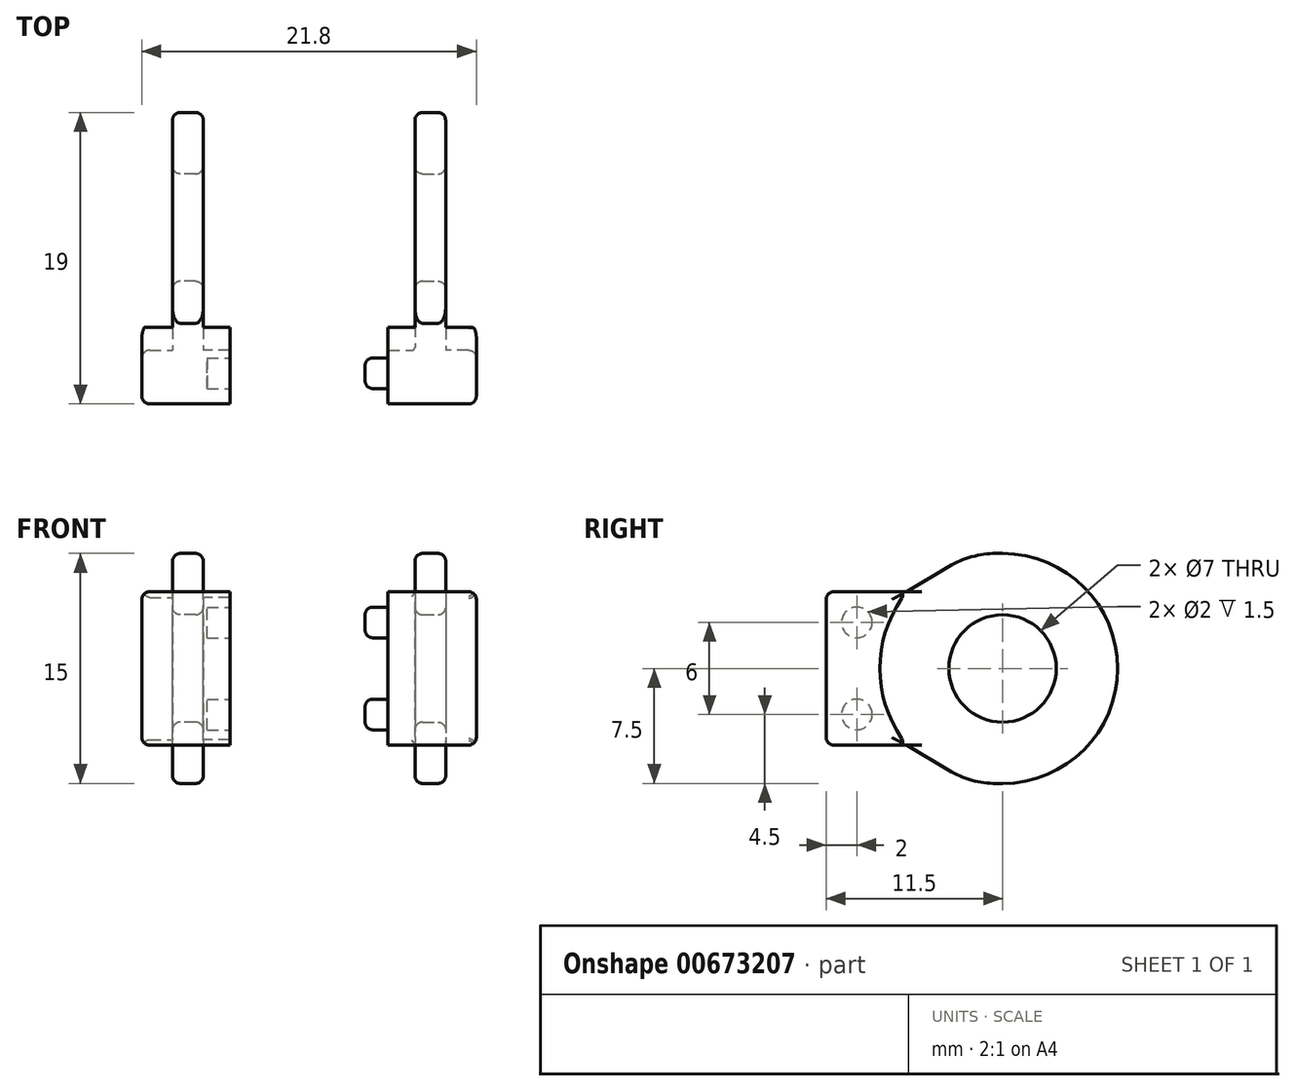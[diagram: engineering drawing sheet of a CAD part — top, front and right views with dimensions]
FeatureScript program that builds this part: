
annotation { "Feature Type Name" : "Feature", "Feature Type Description" : "" }
export const myFeature = defineFeature(function(context is Context, id is Id, definition is map)
    precondition{}
    {
        {
            var Q0;
            Q0=qCreatedBy(makeId("Right.planeOp"),FACE);
            var sketch = newSketch(context, id + "F0", { "sketchPlane" : qUnion([Q0])});
            skArc(sketch, "E0", {"start": v(0, -7.5) * mm, "mid": v(7.5, 0) * mm, "end": v(0, 7.5) * mm});
            skLineSegment(sketch, "E1", {"start": v(0, -7.5) * mm, "end": v(-0.42, -7.5) * mm});
            skLineSegment(sketch, "E2", {"start": v(-10, -5) * mm, "end": v(-10, 5) * mm});
            skLineSegment(sketch, "E3", {"start": v(-0.42, 7.5) * mm, "end": v(0, 7.5) * mm});
            skCircle(sketch, "E4", {"center": v(0, 0) * mm, "radius": 3.5 * mm});
            skCircle(sketch, "E5", {"center": v(0, 0) * mm, "radius": 7.5 * mm, "construction": true});
            skArc(sketch, "E6", {"start": v(-6.52, 4.63) * mm, "mid": v(-8, 0) * mm, "end": v(-6.52, -4.63) * mm});
            skLineSegment(sketch, "E7", {"start": v(-10, 0) * mm, "end": v(-10, 5) * mm, "construction": true});
            skLineSegment(sketch, "E8", {"start": v(-10, 5) * mm, "end": v(-6.24, 5) * mm});
            skLineSegment(sketch, "E9", {"start": v(-6.24, 5) * mm, "end": v(-3.5, 6.65) * mm});
            skLineSegment(sketch, "E10", {"start": v(-10, 0) * mm, "end": v(-13.42, 0) * mm, "construction": true});
            skLineSegment(sketch, "E11.MirrorCS", {"start": v(-10, -5) * mm, "end": v(-6.24, -5) * mm});
            skLineSegment(sketch, "E12.MirrorCS", {"start": v(-6.24, -5) * mm, "end": v(-3.5, -6.65) * mm});
            skPoint(sketch, "E13.start.orphan", {"position": v(-5, -7.5) * mm});
            skPoint(sketch, "E14.orphan", {"position": v(-10, -7.5) * mm});
            skPoint(sketch, "E15.orphan", {"position": v(-10, 7.5) * mm});
            skPoint(sketch, "E16.orphan", {"position": v(-5, 7.5) * mm});
            skPoint(sketch, "E17.visualSharp", {"position": v(-2.08, 7.5) * mm});
            skArc(sketch, "E17.filletArc", {"start": v(-0.42, 7.5) * mm, "mid": v(-2.02, 7.28) * mm, "end": v(-3.5, 6.65) * mm});
            skPoint(sketch, "E18.visualSharp", {"position": v(-2.08, -7.5) * mm});
            skArc(sketch, "E18.filletArc", {"start": v(-3.5, -6.65) * mm, "mid": v(-2.02, -7.28) * mm, "end": v(-0.42, -7.5) * mm});
            skLineSegment(sketch, "E19", {"start": v(-6.52, 5) * mm, "end": v(-6.52, 4.63) * mm});
            skLineSegment(sketch, "E20.MirrorCS", {"start": v(-3.04, 0) * mm, "end": v(0.38, 0) * mm, "construction": true});
            skLineSegment(sketch, "E21.MirrorCS", {"start": v(-6.52, -5) * mm, "end": v(-6.52, -4.63) * mm});
            skSolve(sketch);
        }
        {
            var Q0;
            Q0=makeQuery(id+"F0.imprint","IMPRINT",FACE,{"disambiguationData":[TD([[makeQuery(id+"F0.imprint","IMPRINT",EDGE,{"derivedFrom":sQuery(id+"F0.wireOp",EDGE,"E0")}),1.0]])]});
            var Q1;
            {var subQ1=sQuery(id+"F0.wireOp",EDGE,"E2");Q1=makeQuery(id+"F0.imprint","IMPRINT",FACE,{"disambiguationData":[TD([[makeQuery(id+"F0.imprint","IMPRINT",EDGE,{"derivedFrom":subQ1}),-1.0]])]});}
            extrude(context, id + "F1", {"entities" : qUnion([Q0, Q1]), "depth" : 1 * mm});
        }
        {
            var Q0;
            {var subQ1=sQuery(id+"F0.wireOp",EDGE,"E2");Q0=makeQuery(id+"F0.imprint","IMPRINT",FACE,{"disambiguationData":[TD([[makeQuery(id+"F0.imprint","IMPRINT",EDGE,{"derivedFrom":subQ1}),-1.0]])]});}
            extrude(context, id + "F2", {"entities" : qUnion([Q0]), "operationType" : NewBodyOperationType.ADD, "depth" : 2.75 * mm});
        }
        {
            var Q0;
            {var subQ1=sQuery(id+"F0.wireOp",EDGE,"E2");Q0=makeQuery(id+"F0.imprint","IMPRINT",FACE,{"disambiguationData":[TD([[makeQuery(id+"F0.imprint","IMPRINT",EDGE,{"derivedFrom":subQ1}),-1.0]])]});}
            extrude(context, id + "F3", {"entities" : qUnion([Q0]), "operationType" : NewBodyOperationType.ADD, "oppositeDirection" : true, "depth" : 3 * mm});
        }
        {
            var Q0;
            {var subQ0=sQuery(id+"F0.wireOp",EDGE,"E2");Q0=makeQuery(id+"F3.boolean.opBoolean","MERGE",FACE,{"derivedFrom":[makeQuery(id+"F2.boolean.opBoolean","MERGE",FACE,{"derivedFrom":[makeQuery(id+"F1.opExtrude","SWEPT_FACE",FACE,{"disambiguationData":[OSD([subQ0])]}),makeQuery(id+"F2.opExtrude","SWEPT_FACE",FACE,{"disambiguationData":[OSD([subQ0])]})]}),makeQuery(id+"F3.opExtrude","SWEPT_FACE",FACE,{"disambiguationData":[OSD([subQ0])]})]});}
            extrude(context, id + "F4", {"entities" : qUnion([Q0]), "operationType" : NewBodyOperationType.ADD, "depth" : 1.5 * mm});
        }
        {
            var Q0;
            {var subQ0=sQuery(id+"F0.wireOp",EDGE,"E2");Q0=makeQuery(id+"F4.boolean.opBoolean","MERGE",FACE,{"derivedFrom":[makeQuery(id+"F2.opExtrude","CAP_FACE",FACE,{"disambiguationData":[OSD([sQuery(id+"F0.wireOp",EDGE,"E1"),subQ0,sQuery(id+"F0.wireOp",EDGE,"E3"),sQuery(id+"F0.wireOp",EDGE,"E6"),sQuery(id+"F0.wireOp",EDGE,"eQNor3UN-66I8-VjKn-XfJS-KKaY8PZ4G21v"),sQuery(id+"F0.wireOp",EDGE,"E13")])],"isStart":false}),makeQuery(id+"F4.opExtrude","SWEPT_FACE",FACE,{"disambiguationData":[OSD([subQ0]),TDD([makeQuery(id+"F2.opExtrude","CAP_EDGE",EDGE,{"disambiguationData":[OSD([subQ0])],"isStart":false})])]})]});}
            var sketch = newSketch(context, id + "F5", { "sketchPlane" : qUnion([Q0])});
            skCircle(sketch, "E22", {"center": v(-9.5, 3) * mm, "radius": 1 * mm});
            skLineSegment(sketch, "E23", {"start": v(-8, 0) * mm, "end": v(-11.5, 0) * mm, "construction": true});
            skCircle(sketch, "E24.MirrorC", {"center": v(-9.5, -3) * mm, "radius": 1 * mm});
            skSolve(sketch);
        }
        {
            var Q0;
            Q0=qSketchRegion(id+"F5",true);
            extrude(context, id + "F6", {"entities" : qUnion([Q0]), "operationType" : NewBodyOperationType.REMOVE, "oppositeDirection" : true, "depth" : 1.5 * mm});
        }
        {
            var Q0;
            Q0=qCreatedBy(makeId("Right.planeOp"),FACE);
            cPlane(context, id + "F7", {"entities" : qUnion([Q0]), "cplaneType" : CPlaneType.OFFSET, "offset" : 7.9 * mm, "width" : 150 * mm, "height" : 150 * mm});
        }
        {
            var Q0;
            Q0=makeQuery(id+"F1.opExtrude","SWEPT_BODY",BODY,{"disambiguationData":[OSD([sQuery(id+"F0.wireOp",EDGE,"E0"),sQuery(id+"F0.wireOp",EDGE,"E1"),sQuery(id+"F0.wireOp",EDGE,"E2"),sQuery(id+"F0.wireOp",EDGE,"E3"),sQuery(id+"F0.wireOp",EDGE,"E4")])]});
            var Q1;
            Q1=qCreatedBy(id+"F7.planeOp",FACE);
            mirror(context, id + "F8", {"entities" : qUnion([Q0]), "mirrorPlane" : qUnion([Q1])});
        }
        {
            var Q0;
            Q0=makeQuery(id+"F8.opPattern","COPY",FACE,{"derivedFrom":makeQuery(id+"F6.boolean.opBoolean","COPY",FACE,{"derivedFrom":makeQuery(id+"F6.opExtrude","CAP_FACE",FACE,{"disambiguationData":[OSD([sQuery(id+"F5.wireOp",EDGE,"E22")])],"isStart":false})}),"instanceName":"1"});
            var Q1;
            Q1=makeQuery(id+"F8.opPattern","COPY",FACE,{"derivedFrom":makeQuery(id+"F6.boolean.opBoolean","COPY",FACE,{"derivedFrom":makeQuery(id+"F6.opExtrude","CAP_FACE",FACE,{"disambiguationData":[OSD([sQuery(id+"F5.wireOp",EDGE,"E24.MirrorC")])],"isStart":false})}),"instanceName":"1"});
            extrude(context, id + "F9", {"entities" : qUnion([Q0, Q1]), "operationType" : NewBodyOperationType.ADD, "depth" : 3 * mm});
        }
        {
            var Q0;
            Q0=makeQuery(id+"F1.opExtrude","CAP_FACE",FACE,{"disambiguationData":[OSD([sQuery(id+"F0.wireOp",EDGE,"E0"),sQuery(id+"F0.wireOp",EDGE,"E1"),sQuery(id+"F0.wireOp",EDGE,"E2"),sQuery(id+"F0.wireOp",EDGE,"E3"),sQuery(id+"F0.wireOp",EDGE,"E4")])],"isStart":true});
            extrude(context, id + "F10", {"entities" : qUnion([Q0]), "operationType" : NewBodyOperationType.ADD, "depth" : 1 * mm});
        }
        {
            var Q0;
            Q0=makeQuery(id+"F8.opPattern","COPY",FACE,{"derivedFrom":makeQuery(id+"F1.opExtrude","CAP_FACE",FACE,{"disambiguationData":[OSD([sQuery(id+"F0.wireOp",EDGE,"E0"),sQuery(id+"F0.wireOp",EDGE,"E1"),sQuery(id+"F0.wireOp",EDGE,"E2"),sQuery(id+"F0.wireOp",EDGE,"E3"),sQuery(id+"F0.wireOp",EDGE,"E4")])],"isStart":true}),"instanceName":"1"});
            extrude(context, id + "F11", {"entities" : qUnion([Q0]), "operationType" : NewBodyOperationType.ADD, "depth" : 1 * mm});
        }
        {
            var Q0;
            Q0=makeQuery(id+"F10.opExtrude","CAP_EDGE",EDGE,{"disambiguationData":[OSD([sQuery(id+"F0.wireOp",EDGE,"E0")])],"isStart":false});
            var Q1;
            {var subQ0=sQuery(id+"F0.wireOp",EDGE,"E2");Q1=makeQuery(id+"F4.boolean.opBoolean","MERGE",FACE,{"derivedFrom":[makeQuery(id+"F3.opExtrude","CAP_FACE",FACE,{"disambiguationData":[OSD([subQ0,sQuery(id+"F0.wireOp",EDGE,"E6"),sQuery(id+"F0.wireOp",EDGE,"E8"),sQuery(id+"F0.wireOp",EDGE,"E11.MirrorCS")])],"isStart":false}),makeQuery(id+"F4.opExtrude","SWEPT_FACE",FACE,{"disambiguationData":[OSD([subQ0]),TDD([makeQuery(id+"F3.opExtrude","CAP_EDGE",EDGE,{"disambiguationData":[OSD([subQ0])],"isStart":false})])]})]});}
            var Q2;
            {var subQ0=sQuery(id+"F0.wireOp",EDGE,"E2");Q2=makeQuery(id+"F8.opPattern","COPY",FACE,{"derivedFrom":makeQuery(id+"F4.boolean.opBoolean","MERGE",FACE,{"derivedFrom":[makeQuery(id+"F3.opExtrude","CAP_FACE",FACE,{"disambiguationData":[OSD([subQ0,sQuery(id+"F0.wireOp",EDGE,"E6"),sQuery(id+"F0.wireOp",EDGE,"E8"),sQuery(id+"F0.wireOp",EDGE,"E11.MirrorCS")])],"isStart":false}),makeQuery(id+"F4.opExtrude","SWEPT_FACE",FACE,{"disambiguationData":[OSD([subQ0]),TDD([makeQuery(id+"F3.opExtrude","CAP_EDGE",EDGE,{"disambiguationData":[OSD([subQ0])],"isStart":false})])]})]}),"instanceName":"1"});}
            var Q3;
            Q3=makeQuery(id+"F11.opExtrude","CAP_EDGE",EDGE,{"disambiguationData":[OSD([sQuery(id+"F0.wireOp",EDGE,"E0")])],"isStart":false});
            var Q4;
            Q4=makeQuery(id+"F11.opExtrude","CAP_EDGE",EDGE,{"disambiguationData":[OSD([sQuery(id+"F0.wireOp",EDGE,"E4")])],"isStart":false});
            var Q5;
            Q5=makeQuery(id+"F8.opPattern","COPY",EDGE,{"derivedFrom":makeQuery(id+"F1.opExtrude","CAP_EDGE",EDGE,{"disambiguationData":[OSD([sQuery(id+"F0.wireOp",EDGE,"E4")])],"isStart":false}),"instanceName":"1"});
            var Q6;
            {var subQ0=sQuery(id+"F0.wireOp",EDGE,"E0");Q6=makeQuery(id+"F11.boolean.opBoolean","MERGE",FACE,{"derivedFrom":[makeQuery(id+"F8.opPattern","COPY",FACE,{"derivedFrom":makeQuery(id+"F1.opExtrude","SWEPT_FACE",FACE,{"disambiguationData":[OSD([subQ0])]}),"instanceName":"1"}),makeQuery(id+"F11.opExtrude","SWEPT_FACE",FACE,{"disambiguationData":[OSD([subQ0])]})]});}
            var Q7;
            {var subQ0=sQuery(id+"F0.wireOp",EDGE,"E0");Q7=makeQuery(id+"F10.boolean.opBoolean","MERGE",FACE,{"derivedFrom":[makeQuery(id+"F1.opExtrude","SWEPT_FACE",FACE,{"disambiguationData":[OSD([subQ0])]}),makeQuery(id+"F10.opExtrude","SWEPT_FACE",FACE,{"disambiguationData":[OSD([subQ0])]})]});}
            var Q8;
            Q8=makeQuery(id+"F10.opExtrude","CAP_EDGE",EDGE,{"disambiguationData":[OSD([sQuery(id+"F0.wireOp",EDGE,"E4")])],"isStart":false});
            var Q9;
            Q9=makeQuery(id+"F1.opExtrude","CAP_EDGE",EDGE,{"disambiguationData":[OSD([sQuery(id+"F0.wireOp",EDGE,"E4")])],"isStart":false});
            var Q10;
            Q10=makeQuery(id+"F4.opExtrude","CAP_EDGE",EDGE,{"disambiguationData":[OSD([sQuery(id+"F0.wireOp",EDGE,"E2"),sQuery(id+"F0.wireOp",EDGE,"E8")])],"isStart":false});
            var Q11;
            Q11=makeQuery(id+"F4.opExtrude","CAP_EDGE",EDGE,{"disambiguationData":[OSD([sQuery(id+"F0.wireOp",EDGE,"E2"),sQuery(id+"F0.wireOp",EDGE,"E11.MirrorCS")])],"isStart":false});
            var Q12;
            Q12=makeQuery(id+"F8.opPattern","COPY",EDGE,{"derivedFrom":makeQuery(id+"F4.opExtrude","CAP_EDGE",EDGE,{"disambiguationData":[OSD([sQuery(id+"F0.wireOp",EDGE,"E2"),sQuery(id+"F0.wireOp",EDGE,"E8")])],"isStart":false}),"instanceName":"1"});
            var Q13;
            Q13=makeQuery(id+"F8.opPattern","COPY",EDGE,{"derivedFrom":makeQuery(id+"F4.opExtrude","CAP_EDGE",EDGE,{"disambiguationData":[OSD([sQuery(id+"F0.wireOp",EDGE,"E2"),sQuery(id+"F0.wireOp",EDGE,"E11.MirrorCS")])],"isStart":false}),"instanceName":"1"});
            var Q14;
            Q14=makeQuery(id+"F9.opExtrude","CAP_FACE",FACE,{"disambiguationData":[OSD([sQuery(id+"F5.wireOp",EDGE,"E22")])],"isStart":false});
            var Q15;
            Q15=makeQuery(id+"F9.opExtrude","CAP_FACE",FACE,{"disambiguationData":[OSD([sQuery(id+"F5.wireOp",EDGE,"E24.MirrorC")])],"isStart":false});
            var Q16;
            Q16=makeQuery(id+"F6.boolean.opBoolean","COPY",EDGE,{"derivedFrom":makeQuery(id+"F6.opExtrude","CAP_EDGE",EDGE,{"disambiguationData":[OSD([sQuery(id+"F5.wireOp",EDGE,"E22")])],"isStart":true})});
            var Q17;
            Q17=makeQuery(id+"F6.boolean.opBoolean","COPY",EDGE,{"derivedFrom":makeQuery(id+"F6.opExtrude","CAP_EDGE",EDGE,{"disambiguationData":[OSD([sQuery(id+"F5.wireOp",EDGE,"E24.MirrorC")])],"isStart":true})});
            fillet(context, id + "F12", {"entities" : qUnion([Q0, Q1, Q2, Q3, Q4, Q5, Q6, Q7, Q8, Q9, Q10, Q11, Q12, Q13, Q14, Q15, Q16, Q17]), "radius" : .5 * mm, "tangentPropagation" : true, "allowEdgeOverflow" : false});
        }
        {
            var Q0;
            Q0=makeQuery(id+"F8.opPattern","COPY",EDGE,{"derivedFrom":makeQuery(id+"F2.opExtrude","SWEPT_EDGE",EDGE,{"disambiguationData":[OSD([sQuery(id+"F0.wireOp",EDGE,"E6"),sQuery(id+"F0.wireOp",EDGE,"E19")])]}),"instanceName":"1"});
            var Q1;
            Q1=makeQuery(id+"F8.opPattern","COPY",EDGE,{"derivedFrom":makeQuery(id+"F2.boolean.opBoolean","INTERSECT",EDGE,{"derivedFrom":[makeQuery(id+"F1.opExtrude","CAP_FACE",FACE,{"disambiguationData":[OSD([sQuery(id+"F0.wireOp",EDGE,"E0"),sQuery(id+"F0.wireOp",EDGE,"E1"),sQuery(id+"F0.wireOp",EDGE,"E2"),sQuery(id+"F0.wireOp",EDGE,"E3"),sQuery(id+"F0.wireOp",EDGE,"E4"),sQuery(id+"F0.wireOp",EDGE,"E8"),sQuery(id+"F0.wireOp",EDGE,"E9"),sQuery(id+"F0.wireOp",EDGE,"E11.MirrorCS"),sQuery(id+"F0.wireOp",EDGE,"E12.MirrorCS"),sQuery(id+"F0.wireOp",EDGE,"E17.filletArc"),sQuery(id+"F0.wireOp",EDGE,"E18.filletArc")])],"isStart":false}),makeQuery(id+"F2.opExtrude","SWEPT_FACE",FACE,{"disambiguationData":[OSD([sQuery(id+"F0.wireOp",EDGE,"E6")])]})]}),"instanceName":"1"});
            var Q2;
            Q2=makeQuery(id+"F8.opPattern","COPY",EDGE,{"derivedFrom":makeQuery(id+"F2.opExtrude","SWEPT_EDGE",EDGE,{"disambiguationData":[OSD([sQuery(id+"F0.wireOp",EDGE,"E6"),sQuery(id+"F0.wireOp",EDGE,"E21.MirrorCS")])]}),"instanceName":"1"});
            var Q3;
            Q3=makeQuery(id+"F11.opExtrude","CAP_EDGE",EDGE,{"disambiguationData":[OSD([sQuery(id+"F0.wireOp",EDGE,"E6")])],"isStart":false});
            var Q4;
            Q4=makeQuery(id+"F8.opPattern","COPY",EDGE,{"derivedFrom":makeQuery(id+"F3.opExtrude","SWEPT_EDGE",EDGE,{"disambiguationData":[OSD([sQuery(id+"F0.wireOp",EDGE,"E6"),sQuery(id+"F0.wireOp",EDGE,"E21.MirrorCS")])]}),"instanceName":"1"});
            var Q5;
            Q5=makeQuery(id+"F8.opPattern","COPY",EDGE,{"derivedFrom":makeQuery(id+"F3.opExtrude","SWEPT_EDGE",EDGE,{"disambiguationData":[OSD([sQuery(id+"F0.wireOp",EDGE,"E6"),sQuery(id+"F0.wireOp",EDGE,"E19")])]}),"instanceName":"1"});
            var Q6;
            Q6=makeQuery(id+"F2.boolean.opBoolean","INTERSECT",EDGE,{"derivedFrom":[makeQuery(id+"F1.opExtrude","CAP_FACE",FACE,{"disambiguationData":[OSD([sQuery(id+"F0.wireOp",EDGE,"E0"),sQuery(id+"F0.wireOp",EDGE,"E1"),sQuery(id+"F0.wireOp",EDGE,"E2"),sQuery(id+"F0.wireOp",EDGE,"E3"),sQuery(id+"F0.wireOp",EDGE,"E4"),sQuery(id+"F0.wireOp",EDGE,"E8"),sQuery(id+"F0.wireOp",EDGE,"E9"),sQuery(id+"F0.wireOp",EDGE,"E11.MirrorCS"),sQuery(id+"F0.wireOp",EDGE,"E12.MirrorCS"),sQuery(id+"F0.wireOp",EDGE,"E17.filletArc"),sQuery(id+"F0.wireOp",EDGE,"E18.filletArc")])],"isStart":false}),makeQuery(id+"F2.opExtrude","SWEPT_FACE",FACE,{"disambiguationData":[OSD([sQuery(id+"F0.wireOp",EDGE,"E6")])]})]});
            var Q7;
            Q7=makeQuery(id+"F2.opExtrude","SWEPT_EDGE",EDGE,{"disambiguationData":[OSD([sQuery(id+"F0.wireOp",EDGE,"E6"),sQuery(id+"F0.wireOp",EDGE,"E19")])]});
            var Q8;
            Q8=makeQuery(id+"F2.opExtrude","SWEPT_EDGE",EDGE,{"disambiguationData":[OSD([sQuery(id+"F0.wireOp",EDGE,"E6"),sQuery(id+"F0.wireOp",EDGE,"E21.MirrorCS")])]});
            var Q9;
            Q9=makeQuery(id+"F10.opExtrude","CAP_EDGE",EDGE,{"disambiguationData":[OSD([sQuery(id+"F0.wireOp",EDGE,"E6")])],"isStart":false});
            var Q10;
            Q10=makeQuery(id+"F3.opExtrude","SWEPT_EDGE",EDGE,{"disambiguationData":[OSD([sQuery(id+"F0.wireOp",EDGE,"E6"),sQuery(id+"F0.wireOp",EDGE,"E21.MirrorCS")])]});
            var Q11;
            Q11=makeQuery(id+"F3.opExtrude","SWEPT_EDGE",EDGE,{"disambiguationData":[OSD([sQuery(id+"F0.wireOp",EDGE,"E6"),sQuery(id+"F0.wireOp",EDGE,"E19")])]});
            fillet(context, id + "F13", {"entities" : qUnion([Q0, Q1, Q2, Q3, Q4, Q5, Q6, Q7, Q8, Q9, Q10, Q11]), "radius" : .2 * mm, "tangentPropagation" : true, "allowEdgeOverflow" : false});
        }
    });
